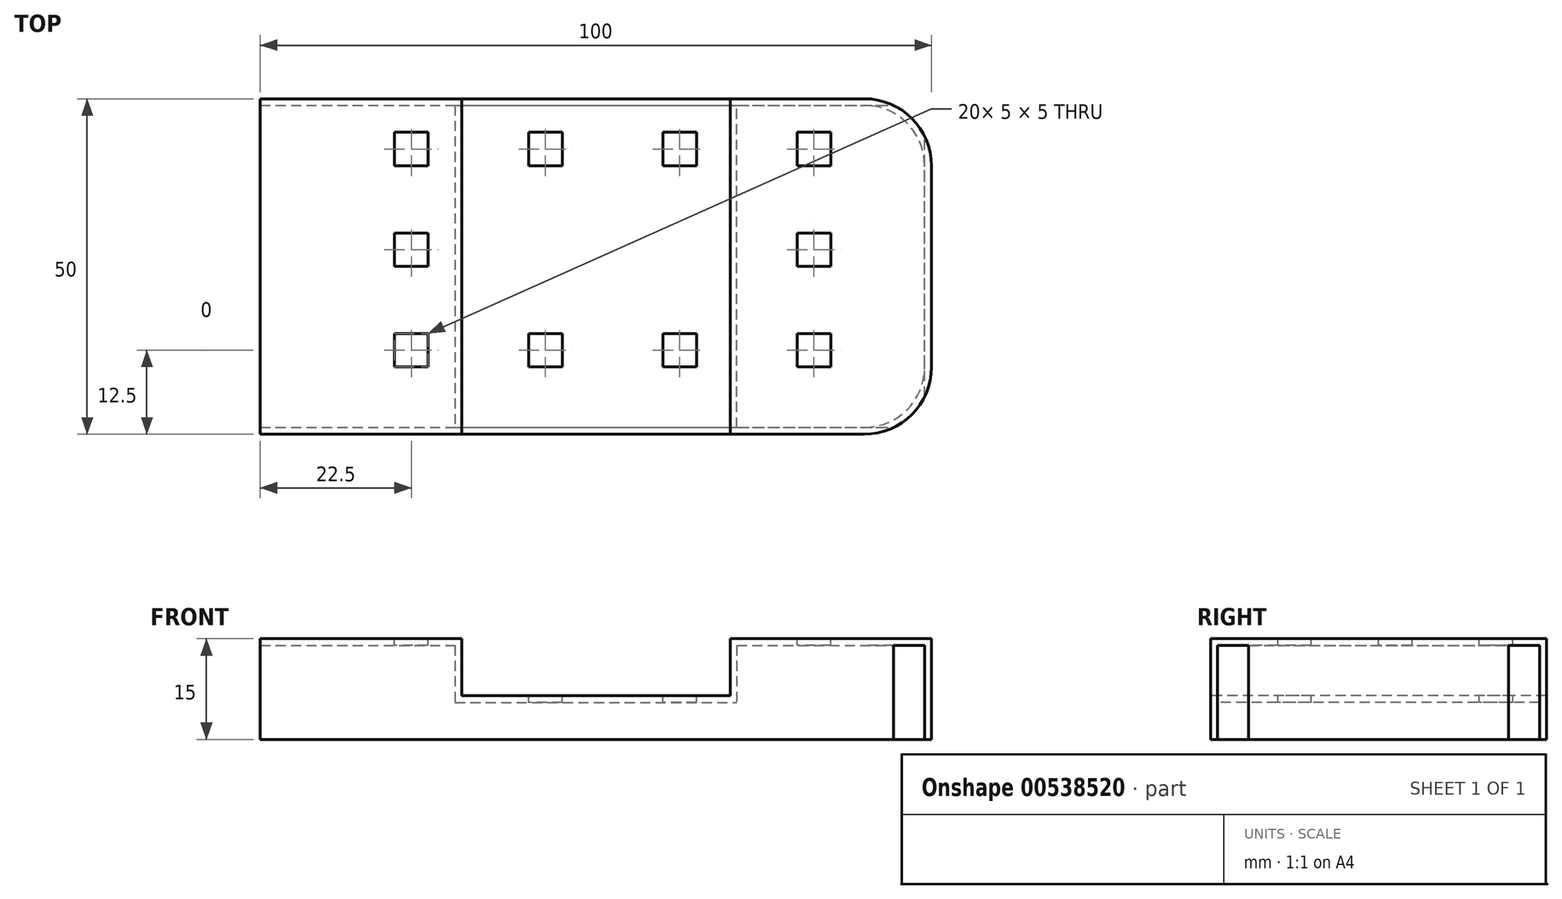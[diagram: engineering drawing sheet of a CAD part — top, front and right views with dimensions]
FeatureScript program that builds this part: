
annotation { "Feature Type Name" : "Feature", "Feature Type Description" : "" }
export const myFeature = defineFeature(function(context is Context, id is Id, definition is map)
    precondition{}
    {
        {
            var Q0;
            Q0=qCreatedBy(makeId("Top.planeOp"),FACE);
            var sketch = newSketch(context, id + "F0", { "sketchPlane" : qUnion([Q0])});
            skLineSegment(sketch, "E0.bottom", {"start": v(0, 0) * mm, "end": v(-100, 0) * mm});
            skLineSegment(sketch, "E0.top", {"start": v(0, 50) * mm, "end": v(-100, 50) * mm});
            skLineSegment(sketch, "E0.left", {"start": v(0, 0) * mm, "end": v(0, 50) * mm});
            skLineSegment(sketch, "E0.right", {"start": v(-100, 0) * mm, "end": v(-100, 50) * mm});
            skSolve(sketch);
        }
        {
            var Q0;
            Q0=makeQuery(id+"F0.imprint","IMPRINT",FACE,{"disambiguationData":[TD([[makeQuery(id+"F0.imprint","IMPRINT",EDGE,{"derivedFrom":sQuery(id+"F0.wireOp",EDGE,"E0.bottom")}),-1.0]])]});
            extrude(context, id + "F1", {"entities" : qUnion([Q0]), "depth" : 15 * mm, "offsetDistance" : 25 * mm});
        }
        {
            var Q0;
            Q0=makeQuery(id+"F1.opExtrude","CAP_FACE",FACE,{"disambiguationData":[OSD([sQuery(id+"F0.wireOp",EDGE,"E0.bottom"),sQuery(id+"F0.wireOp",EDGE,"E0.top"),sQuery(id+"F0.wireOp",EDGE,"E0.left"),sQuery(id+"F0.wireOp",EDGE,"E0.right")])],"isStart":false});
            var sketch = newSketch(context, id + "F2", { "sketchPlane" : qUnion([Q0])});
            skLineSegment(sketch, "E1", {"start": v(0, 50) * mm, "end": v(-30, 50) * mm});
            skLineSegment(sketch, "E2", {"start": v(-30, 50) * mm, "end": v(-70, 50) * mm});
            skLineSegment(sketch, "E3", {"start": v(-70, 50) * mm, "end": v(-70, 0) * mm});
            skLineSegment(sketch, "E4", {"start": v(-30, 50) * mm, "end": v(-30, 0) * mm});
            skLineSegment(sketch, "E5", {"start": v(-30, 0) * mm, "end": v(-70, 0) * mm});
            skLineSegment(sketch, "E6", {"start": v(0, 50) * mm, "end": v(-15, 50) * mm});
            skLineSegment(sketch, "E7", {"start": v(-15, 50) * mm, "end": v(-15, 45) * mm});
            skLineSegment(sketch, "E8.bottom", {"start": v(-15, 45) * mm, "end": v(-20, 45) * mm});
            skLineSegment(sketch, "E8.top", {"start": v(-15, 40) * mm, "end": v(-20, 40) * mm});
            skLineSegment(sketch, "E8.left", {"start": v(-15, 45) * mm, "end": v(-15, 40) * mm});
            skLineSegment(sketch, "E8.right", {"start": v(-20, 45) * mm, "end": v(-20, 40) * mm});
            skLineSegment(sketch, "E9", {"start": v(-15, 40) * mm, "end": v(-15, 35) * mm});
            skLineSegment(sketch, "E10", {"start": v(-20, 45) * mm, "end": v(-30, 45) * mm});
            skLineSegment(sketch, "E11.1.0.0", {"start": v(-40, 45) * mm, "end": v(-40, 40) * mm});
            skLineSegment(sketch, "E11.1.0.1", {"start": v(-35, 45) * mm, "end": v(-40, 45) * mm});
            skLineSegment(sketch, "E11.1.0.2", {"start": v(-35, 45) * mm, "end": v(-35, 40) * mm});
            skLineSegment(sketch, "E11.1.0.3", {"start": v(-35, 40) * mm, "end": v(-40, 40) * mm});
            skLineSegment(sketch, "E11.2.0.0", {"start": v(-60, 45) * mm, "end": v(-60, 40) * mm});
            skLineSegment(sketch, "E11.2.0.1", {"start": v(-55, 45) * mm, "end": v(-60, 45) * mm});
            skLineSegment(sketch, "E11.2.0.2", {"start": v(-55, 45) * mm, "end": v(-55, 40) * mm});
            skLineSegment(sketch, "E11.2.0.3", {"start": v(-55, 40) * mm, "end": v(-60, 40) * mm});
            skLineSegment(sketch, "E11.3.0.0", {"start": v(-80, 45) * mm, "end": v(-80, 40) * mm});
            skLineSegment(sketch, "E11.3.0.1", {"start": v(-75, 45) * mm, "end": v(-80, 45) * mm});
            skLineSegment(sketch, "E11.3.0.2", {"start": v(-75, 45) * mm, "end": v(-75, 40) * mm});
            skLineSegment(sketch, "E11.3.0.3", {"start": v(-75, 40) * mm, "end": v(-80, 40) * mm});
            skLineSegment(sketch, "E11.direction1", {"start": v(-20, 40) * mm, "end": v(-40, 40) * mm, "construction": true});
            skLineSegment(sketch, "E12.0.1.0", {"start": v(-15, 25) * mm, "end": v(-20, 25) * mm});
            skLineSegment(sketch, "E12.0.1.1", {"start": v(-20, 30) * mm, "end": v(-20, 25) * mm});
            skLineSegment(sketch, "E12.0.1.2", {"start": v(-15, 30) * mm, "end": v(-20, 30) * mm});
            skLineSegment(sketch, "E12.0.1.3", {"start": v(-15, 30) * mm, "end": v(-15, 25) * mm});
            skLineSegment(sketch, "E12.0.2.0", {"start": v(-15, 10) * mm, "end": v(-20, 10) * mm});
            skLineSegment(sketch, "E12.0.2.1", {"start": v(-20, 15) * mm, "end": v(-20, 10) * mm});
            skLineSegment(sketch, "E12.0.2.2", {"start": v(-15, 15) * mm, "end": v(-20, 15) * mm});
            skLineSegment(sketch, "E12.0.2.3", {"start": v(-15, 15) * mm, "end": v(-15, 10) * mm});
            skLineSegment(sketch, "E12.direction1", {"start": v(-20, 40) * mm, "end": v(0, 40) * mm, "construction": true});
            skLineSegment(sketch, "E12.direction2", {"start": v(-20, 40) * mm, "end": v(-20, 25) * mm, "construction": true});
            skLineSegment(sketch, "E13.1.0.0", {"start": v(-35, 15) * mm, "end": v(-35, 10) * mm});
            skLineSegment(sketch, "E13.1.0.1", {"start": v(-35, 15) * mm, "end": v(-40, 15) * mm});
            skLineSegment(sketch, "E13.1.0.2", {"start": v(-40, 15) * mm, "end": v(-40, 10) * mm});
            skLineSegment(sketch, "E13.1.0.3", {"start": v(-35, 10) * mm, "end": v(-40, 10) * mm});
            skLineSegment(sketch, "E13.2.0.0", {"start": v(-55, 15) * mm, "end": v(-55, 10) * mm});
            skLineSegment(sketch, "E13.2.0.1", {"start": v(-55, 15) * mm, "end": v(-60, 15) * mm});
            skLineSegment(sketch, "E13.2.0.2", {"start": v(-60, 15) * mm, "end": v(-60, 10) * mm});
            skLineSegment(sketch, "E13.2.0.3", {"start": v(-55, 10) * mm, "end": v(-60, 10) * mm});
            skLineSegment(sketch, "E13.3.0.0", {"start": v(-75, 15) * mm, "end": v(-75, 10) * mm});
            skLineSegment(sketch, "E13.3.0.1", {"start": v(-75, 15) * mm, "end": v(-80, 15) * mm});
            skLineSegment(sketch, "E13.3.0.2", {"start": v(-80, 15) * mm, "end": v(-80, 10) * mm});
            skLineSegment(sketch, "E13.3.0.3", {"start": v(-75, 10) * mm, "end": v(-80, 10) * mm});
            skLineSegment(sketch, "E13.direction1", {"start": v(-15, 10) * mm, "end": v(-35, 10) * mm, "construction": true});
            skLineSegment(sketch, "E14", {"start": v(-75, 15) * mm, "end": v(-75, 20) * mm});
            skLineSegment(sketch, "E15.0.1.0", {"start": v(-75, 30) * mm, "end": v(-80, 30) * mm});
            skLineSegment(sketch, "E15.0.1.1", {"start": v(-80, 30) * mm, "end": v(-80, 25) * mm});
            skLineSegment(sketch, "E15.0.1.2", {"start": v(-75, 25) * mm, "end": v(-80, 25) * mm});
            skLineSegment(sketch, "E15.0.1.3", {"start": v(-75, 30) * mm, "end": v(-75, 25) * mm});
            skLineSegment(sketch, "E15.direction1", {"start": v(-80, 15) * mm, "end": v(-60, 15) * mm, "construction": true});
            skLineSegment(sketch, "E15.direction2", {"start": v(-80, 15) * mm, "end": v(-80, 30) * mm, "construction": true});
            skSolve(sketch);
        }
        {
            var Q0;
            Q0=makeQuery(id+"F2.imprint","IMPRINT",FACE,{"disambiguationData":[TD([[makeQuery(id+"F2.imprint","IMPRINT",EDGE,{"derivedFrom":sQuery(id+"F2.wireOp",EDGE,"E2")}),1.0]])]});
            extrude(context, id + "F3", {"entities" : qUnion([Q0]), "operationType" : NewBodyOperationType.REMOVE, "oppositeDirection" : true, "depth" : 8.5 * mm, "offsetDistance" : 25 * mm});
        }
        {
            var Q0;
            Q0=makeQuery(id+"F2.imprint","IMPRINT",FACE,{"disambiguationData":[TD([[makeQuery(id+"F2.imprint","IMPRINT",EDGE,{"derivedFrom":sQuery(id+"F2.wireOp",EDGE,"E11.3.0.0")}),1.0]])]});
            var Q1;
            Q1=makeQuery(id+"F2.imprint","IMPRINT",FACE,{"disambiguationData":[TD([[makeQuery(id+"F2.imprint","IMPRINT",EDGE,{"derivedFrom":sQuery(id+"F2.wireOp",EDGE,"E15.0.1.0")}),1.0]])]});
            var Q2;
            Q2=makeQuery(id+"F2.imprint","IMPRINT",FACE,{"disambiguationData":[TD([[makeQuery(id+"F2.imprint","IMPRINT",EDGE,{"derivedFrom":sQuery(id+"F2.wireOp",EDGE,"E13.3.0.0")}),-1.0]])]});
            var Q3;
            Q3=makeQuery(id+"F2.imprint","IMPRINT",FACE,{"disambiguationData":[TD([[makeQuery(id+"F2.imprint","IMPRINT",EDGE,{"derivedFrom":sQuery(id+"F2.wireOp",EDGE,"E13.2.0.0")}),-1.0]])]});
            var Q4;
            Q4=makeQuery(id+"F2.imprint","IMPRINT",FACE,{"disambiguationData":[TD([[makeQuery(id+"F2.imprint","IMPRINT",EDGE,{"derivedFrom":sQuery(id+"F2.wireOp",EDGE,"E11.2.0.0")}),1.0]])]});
            var Q5;
            Q5=makeQuery(id+"F2.imprint","IMPRINT",FACE,{"disambiguationData":[TD([[makeQuery(id+"F2.imprint","IMPRINT",EDGE,{"derivedFrom":sQuery(id+"F2.wireOp",EDGE,"E11.1.0.0")}),1.0]])]});
            var Q6;
            Q6=makeQuery(id+"F2.imprint","IMPRINT",FACE,{"disambiguationData":[TD([[makeQuery(id+"F2.imprint","IMPRINT",EDGE,{"derivedFrom":sQuery(id+"F2.wireOp",EDGE,"E13.1.0.0")}),-1.0]])]});
            var Q7;
            Q7=makeQuery(id+"F2.imprint","IMPRINT",FACE,{"disambiguationData":[TD([[makeQuery(id+"F2.imprint","IMPRINT",EDGE,{"derivedFrom":sQuery(id+"F2.wireOp",EDGE,"E12.0.2.0")}),-1.0]])]});
            var Q8;
            Q8=makeQuery(id+"F2.imprint","IMPRINT",FACE,{"disambiguationData":[TD([[makeQuery(id+"F2.imprint","IMPRINT",EDGE,{"derivedFrom":sQuery(id+"F2.wireOp",EDGE,"E12.0.1.0")}),-1.0]])]});
            var Q9;
            Q9=makeQuery(id+"F2.imprint","IMPRINT",FACE,{"disambiguationData":[TD([[makeQuery(id+"F2.imprint","IMPRINT",EDGE,{"derivedFrom":sQuery(id+"F2.wireOp",EDGE,"E8.bottom")}),1.0]])]});
            extrude(context, id + "F4", {"entities" : qUnion([Q0, Q1, Q2, Q3, Q4, Q5, Q6, Q7, Q8, Q9]), "operationType" : NewBodyOperationType.REMOVE, "endBound" : BoundingType.THROUGH_ALL, "oppositeDirection" : true, "depth" : 25 * mm, "offsetDistance" : 25 * mm});
        }
        {
            var Q0;
            Q0=makeQuery(id+"F1.opExtrude","CAP_FACE",FACE,{"disambiguationData":[OSD([sQuery(id+"F0.wireOp",EDGE,"E0.bottom"),sQuery(id+"F0.wireOp",EDGE,"E0.top"),sQuery(id+"F0.wireOp",EDGE,"E0.left"),sQuery(id+"F0.wireOp",EDGE,"E0.right")])],"isStart":true});
            var sketch = newSketch(context, id + "F5", { "sketchPlane" : qUnion([Q0])});
            skLineSegment(sketch, "E16", {"start": v(-100, 0) * mm, "end": v(-100, -1) * mm});
            skLineSegment(sketch, "E17", {"start": v(-100, -50) * mm, "end": v(-100, -49) * mm});
            skLineSegment(sketch, "E18", {"start": v(-100, -50) * mm, "end": v(-71, -50) * mm});
            skLineSegment(sketch, "E19", {"start": v(-71, -50) * mm, "end": v(-71, 0) * mm});
            skLineSegment(sketch, "E20", {"start": v(-71, 0) * mm, "end": v(-100, 0) * mm});
            skLineSegment(sketch, "E21", {"start": v(-100, -1) * mm, "end": v(-71, -1) * mm});
            skLineSegment(sketch, "E22", {"start": v(-100, -49) * mm, "end": v(-71, -49) * mm});
            skLineSegment(sketch, "E23", {"start": v(-71, -1) * mm, "end": v(-29, -1) * mm});
            skLineSegment(sketch, "E24", {"start": v(-29, -1) * mm, "end": v(-29, -50) * mm});
            skLineSegment(sketch, "E25", {"start": v(-71, -50) * mm, "end": v(-29, -50) * mm});
            skLineSegment(sketch, "E26", {"start": v(-29, -1) * mm, "end": v(-29, 0) * mm});
            skLineSegment(sketch, "E27", {"start": v(-29, 0) * mm, "end": v(-71, 0) * mm});
            skLineSegment(sketch, "E28", {"start": v(-29, -1) * mm, "end": v(-1, -1) * mm});
            skLineSegment(sketch, "E29", {"start": v(-1, -1) * mm, "end": v(-1, -50) * mm});
            skLineSegment(sketch, "E30", {"start": v(-1, -50) * mm, "end": v(-29, -50) * mm});
            skLineSegment(sketch, "E31", {"start": v(-71, -49) * mm, "end": v(-29, -49) * mm});
            skLineSegment(sketch, "E32", {"start": v(-29, -49) * mm, "end": v(-1, -49) * mm});
            skSolve(sketch);
        }
        {
            var Q0;
            {var subQ1=sQuery(id+"F5.wireOp",EDGE,"E28");Q0=makeQuery(id+"F5.imprint","IMPRINT",FACE,{"disambiguationData":[TD([[makeQuery(id+"F5.imprint","IMPRINT",EDGE,{"derivedFrom":subQ1}),-1.0]])]});}
            var Q1;
            {var subQ2=sQuery(id+"F5.wireOp",EDGE,"E21");Q1=makeQuery(id+"F5.imprint","IMPRINT",FACE,{"disambiguationData":[TD([[makeQuery(id+"F5.imprint","IMPRINT",EDGE,{"derivedFrom":subQ2}),-1.0]])]});}
            extrude(context, id + "F6", {"entities" : qUnion([Q0, Q1]), "operationType" : NewBodyOperationType.REMOVE, "oppositeDirection" : true, "depth" : 14 * mm, "offsetDistance" : 25 * mm});
        }
        {
            var Q0;
            {var subQ2=sQuery(id+"F5.wireOp",EDGE,"E23");Q0=makeQuery(id+"F5.imprint","IMPRINT",FACE,{"disambiguationData":[TD([[makeQuery(id+"F5.imprint","IMPRINT",EDGE,{"derivedFrom":subQ2}),-1.0]])]});}
            extrude(context, id + "F7", {"entities" : qUnion([Q0]), "operationType" : NewBodyOperationType.REMOVE, "oppositeDirection" : true, "depth" : 5.5 * mm, "offsetDistance" : 25 * mm});
        }
        {
            var Q0;
            Q0=makeQuery(id+"F6.boolean.opBoolean","COPY",EDGE,{"derivedFrom":makeQuery(id+"F6.opExtrude","SWEPT_EDGE",EDGE,{"disambiguationData":[OSD([sQuery(id+"F5.wireOp",EDGE,"E29"),sQuery(id+"F5.wireOp",EDGE,"E32")])]})});
            var Q1;
            Q1=makeQuery(id+"F6.boolean.opBoolean","COPY",EDGE,{"derivedFrom":makeQuery(id+"F6.opExtrude","SWEPT_EDGE",EDGE,{"disambiguationData":[OSD([sQuery(id+"F5.wireOp",EDGE,"E28"),sQuery(id+"F5.wireOp",EDGE,"E29")])]})});
            fillet(context, id + "F8", {"entities" : qUnion([Q0, Q1]), "radius" : 9 * mm, "tangentPropagation" : true, "allowEdgeOverflow" : false});
        }
        {
            var Q0;
            Q0=makeQuery(id+"F1.opExtrude","SWEPT_EDGE",EDGE,{"disambiguationData":[OSD([sQuery(id+"F0.wireOp",EDGE,"E0.top"),sQuery(id+"F0.wireOp",EDGE,"E0.left")])]});
            var Q1;
            Q1=makeQuery(id+"F1.opExtrude","SWEPT_EDGE",EDGE,{"disambiguationData":[OSD([sQuery(id+"F0.wireOp",EDGE,"E0.bottom"),sQuery(id+"F0.wireOp",EDGE,"E0.left")])]});
            fillet(context, id + "F9", {"entities" : qUnion([Q0, Q1]), "radius" : 10 * mm, "tangentPropagation" : true, "allowEdgeOverflow" : false});
        }
    });
